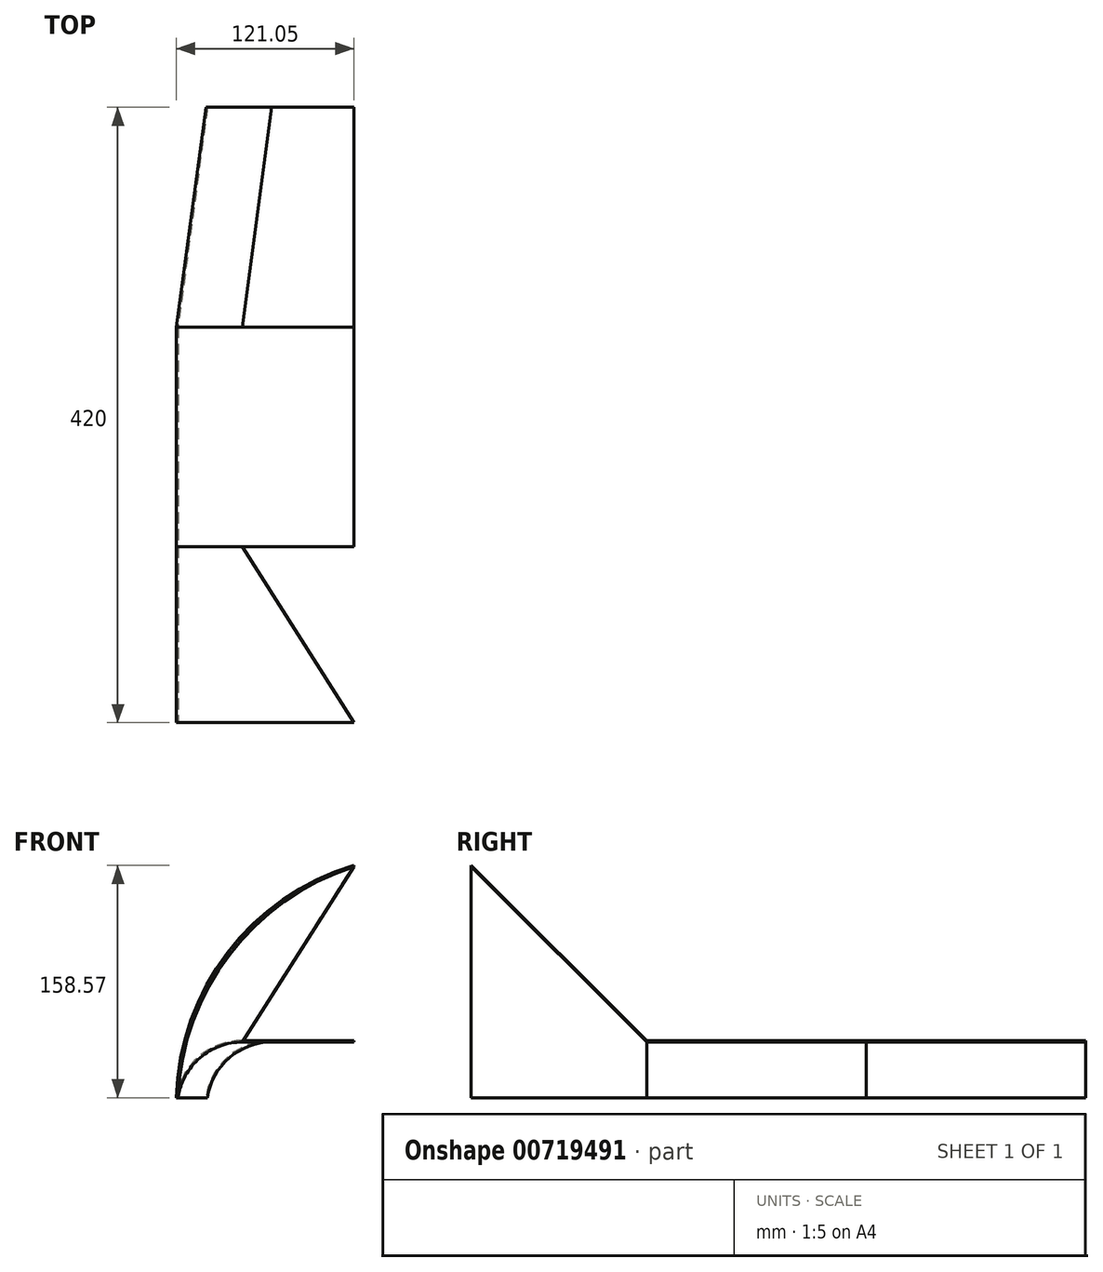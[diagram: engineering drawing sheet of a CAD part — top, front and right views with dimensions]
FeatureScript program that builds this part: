
annotation { "Feature Type Name" : "Feature", "Feature Type Description" : "" }
export const myFeature = defineFeature(function(context is Context, id is Id, definition is map)
    precondition{}
    {
        {
            var Q0;
            Q0=qCreatedBy(makeId("Front.planeOp"),FACE);
            var sketch = newSketch(context, id + "F0", { "sketchPlane" : qUnion([Q0])});
            skLineSegment(sketch, "E0", {"start": v(-55.95, 38) * mm, "end": v(0, 38) * mm});
            skArc(sketch, "E1", {"start": v(-55.95, 38) * mm, "mid": v(-85.05, 27.19) * mm, "end": v(-100.02, 0) * mm});
            skLineSegment(sketch, "E2", {"start": v(0, 38) * mm, "end": v(0, 39.02) * mm});
            skLineSegment(sketch, "E3", {"start": v(0, 39.02) * mm, "end": v(-55.95, 39.02) * mm});
            skLineSegment(sketch, "E4", {"start": v(-100.02, 0) * mm, "end": v(-101.02, 0) * mm});
            skArc(sketch, "E5", {"start": v(-55.95, 39.02) * mm, "mid": v(-85.76, 27.9) * mm, "end": v(-101.02, 0) * mm});
            skSolve(sketch);
        }
        {
            var Q0;
            Q0=qCreatedBy(makeId("Front.planeOp"),FACE);
            cPlane(context, id + "F1", {"entities" : qUnion([Q0]), "cplaneType" : CPlaneType.OFFSET, "offset" : 150 * mm, "width" : 150 * mm, "height" : 150 * mm});
        }
        {
            var Q0;
            Q0=qCreatedBy(id+"F1.planeOp",FACE);
            var sketch = newSketch(context, id + "F2", { "sketchPlane" : qUnion([Q0])});
            skLineSegment(sketch, "E6", {"start": v(-75.95, 38) * mm, "end": v(0, 38) * mm});
            skArc(sketch, "E7", {"start": v(-75.95, 38) * mm, "mid": v(-105.05, 27.2) * mm, "end": v(-120.03, 0) * mm});
            skLineSegment(sketch, "E8", {"start": v(0, 38) * mm, "end": v(0, 39.02) * mm});
            skLineSegment(sketch, "E9", {"start": v(0, 39.02) * mm, "end": v(-75.95, 39.02) * mm});
            skLineSegment(sketch, "E10", {"start": v(-120.03, 0) * mm, "end": v(-121.04, 0) * mm});
            skArc(sketch, "E11", {"start": v(-75.95, 39.02) * mm, "mid": v(-105.77, 27.9) * mm, "end": v(-121.04, 0) * mm});
            skSolve(sketch);
        }
        {
            var Q0;
            Q0 = qSketchRegion(id + "F0", true);
            var Q1;
            Q1 = qSketchRegion(id + "F2", true);
            loft(context, id + "F3", {"sheetProfilesArray" : [{ "sheetProfileEntities" : qUnion([Q0]) }, { "sheetProfileEntities" : qUnion([Q1]) }]});
        }
        {
            var Q0;
            Q0=qCreatedBy(id+"F1.planeOp",FACE);
            cPlane(context, id + "F4", {"entities" : qUnion([Q0]), "cplaneType" : CPlaneType.OFFSET, "offset" : 150 * mm, "width" : 150 * mm, "height" : 150 * mm});
        }
        {
            var Q0;
            Q0=qCreatedBy(id+"F4.planeOp",FACE);
            var sketch = newSketch(context, id + "F5", { "sketchPlane" : qUnion([Q0])});
            skLineSegment(sketch, "E12", {"start": v(-75.95, 38) * mm, "end": v(0, 38) * mm});
            skArc(sketch, "E13", {"start": v(-75.95, 38) * mm, "mid": v(-105.05, 27.2) * mm, "end": v(-120.02, 0.01) * mm});
            skLineSegment(sketch, "E14", {"start": v(0, 38) * mm, "end": v(0, 39.02) * mm});
            skLineSegment(sketch, "E15", {"start": v(0, 39.02) * mm, "end": v(-75.95, 39.02) * mm});
            skLineSegment(sketch, "E16", {"start": v(-120.02, 0.01) * mm, "end": v(-121.04, 0.01) * mm});
            skArc(sketch, "E17", {"start": v(-75.95, 39.02) * mm, "mid": v(-105.76, 27.91) * mm, "end": v(-121.04, 0.01) * mm});
            skSolve(sketch);
        }
        {
            var Q0;
            Q0 = qSketchRegion(id + "F5", true);
            extrude(context, id + "F6", {"entities" : qUnion([Q0]), "oppositeDirection" : true, "depth" : 150 * mm, "offsetDistance" : 25 * mm});
        }
        {
            var Q0;
            Q0=qCreatedBy(id+"F4.planeOp",FACE);
            cPlane(context, id + "F7", {"entities" : qUnion([Q0]), "cplaneType" : CPlaneType.OFFSET, "offset" : 120 * mm, "width" : 150 * mm, "height" : 150 * mm});
        }
        {
            var Q0;
            Q0=qCreatedBy(id+"F7.planeOp",FACE);
            var sketch = newSketch(context, id + "F8", { "sketchPlane" : qUnion([Q0])});
            skArc(sketch, "E18", {"start": v(0, 158.57) * mm, "mid": v(-86.25, 98.92) * mm, "end": v(-121.05, 0) * mm});
            skPoint(sketch, "E19", {"position": v(-121.05, 0) * mm});
            skLineSegment(sketch, "E20", {"start": v(-121.05, 0) * mm, "end": v(-120.01, 0) * mm});
            skLineSegment(sketch, "E21", {"start": v(0, 158.57) * mm, "end": v(0, 157.54) * mm});
            skArc(sketch, "E22", {"start": v(0, 157.54) * mm, "mid": v(-84.83, 97.68) * mm, "end": v(-120.01, 0) * mm});
            skSolve(sketch);
        }
        {
            var Q0;
            Q0=qCreatedBy(makeId("Right.planeOp"),FACE);
            var sketch = newSketch(context, id + "F9", { "sketchPlane" : qUnion([Q0])});
            skArc(sketch, "E23", {"start": v(-419.98, 158.57) * mm, "mid": v(-384.68, 74.01) * mm, "end": v(-300, 39.02) * mm});
            skLineSegment(sketch, "E24", {"start": v(-300, 39.02) * mm, "end": v(-300, 38.01) * mm});
            skLineSegment(sketch, "E25", {"start": v(-419.98, 158.57) * mm, "end": v(-420.99, 158.57) * mm});
            skArc(sketch, "E26", {"start": v(-420.99, 158.57) * mm, "mid": v(-385.44, 73.25) * mm, "end": v(-300, 38.01) * mm});
            skSolve(sketch);
        }
        {
            var Q0;
            Q0 = qSketchRegion(id + "F9", true);
            extrude(context, id + "F10", {"entities" : qUnion([Q0]), "operationType" : NewBodyOperationType.REMOVE, "oppositeDirection" : true, "depth" : 76 * mm, "offsetDistance" : 25 * mm});
        }
        {
            var Q0;
            Q0=qCreatedBy(id+"F7.planeOp",FACE);
            cPlane(context, id + "F11", {"entities" : qUnion([Q0]), "cplaneType" : CPlaneType.OFFSET, "offset" : 120 * mm, "oppositeDirection" : true, "width" : 150 * mm, "height" : 150 * mm});
        }
        {
            var Q0;
            Q0=qCreatedBy(id+"F11.planeOp",FACE);
            var sketch = newSketch(context, id + "F12", { "sketchPlane" : qUnion([Q0])});
            skArc(sketch, "E27", {"start": v(-75.95, 38) * mm, "mid": v(-105.04, 27.19) * mm, "end": v(-120.02, 0) * mm});
            skLineSegment(sketch, "E28", {"start": v(-120.02, 0) * mm, "end": v(-121.04, 0) * mm});
            skArc(sketch, "E29", {"start": v(-75.95, 39) * mm, "mid": v(-105.76, 27.9) * mm, "end": v(-121.04, 0) * mm});
            skLineSegment(sketch, "E30", {"start": v(-75.95, 39) * mm, "end": v(-75.95, 38) * mm});
            skSolve(sketch);
        }
        {
            var Q1;
            Q1 = qSketchRegion(id + "F12", true);
            var Q2;
            Q2=makeQuery(id+"F8.imprint","IMPRINT",FACE,{"disambiguationData":[TD([[makeQuery(id+"F8.imprint","IMPRINT",EDGE,{"derivedFrom":sQuery(id+"F8.wireOp",EDGE,"E18")}),1.0]])]});
            loft(context, id + "F13", {"operationType" : NewBodyOperationType.ADD, "sheetProfilesArray" : [{ "sheetProfileEntities" : qUnion([Q1]) }, { "sheetProfileEntities" : qUnion([Q2]) }]});
        }
    });
